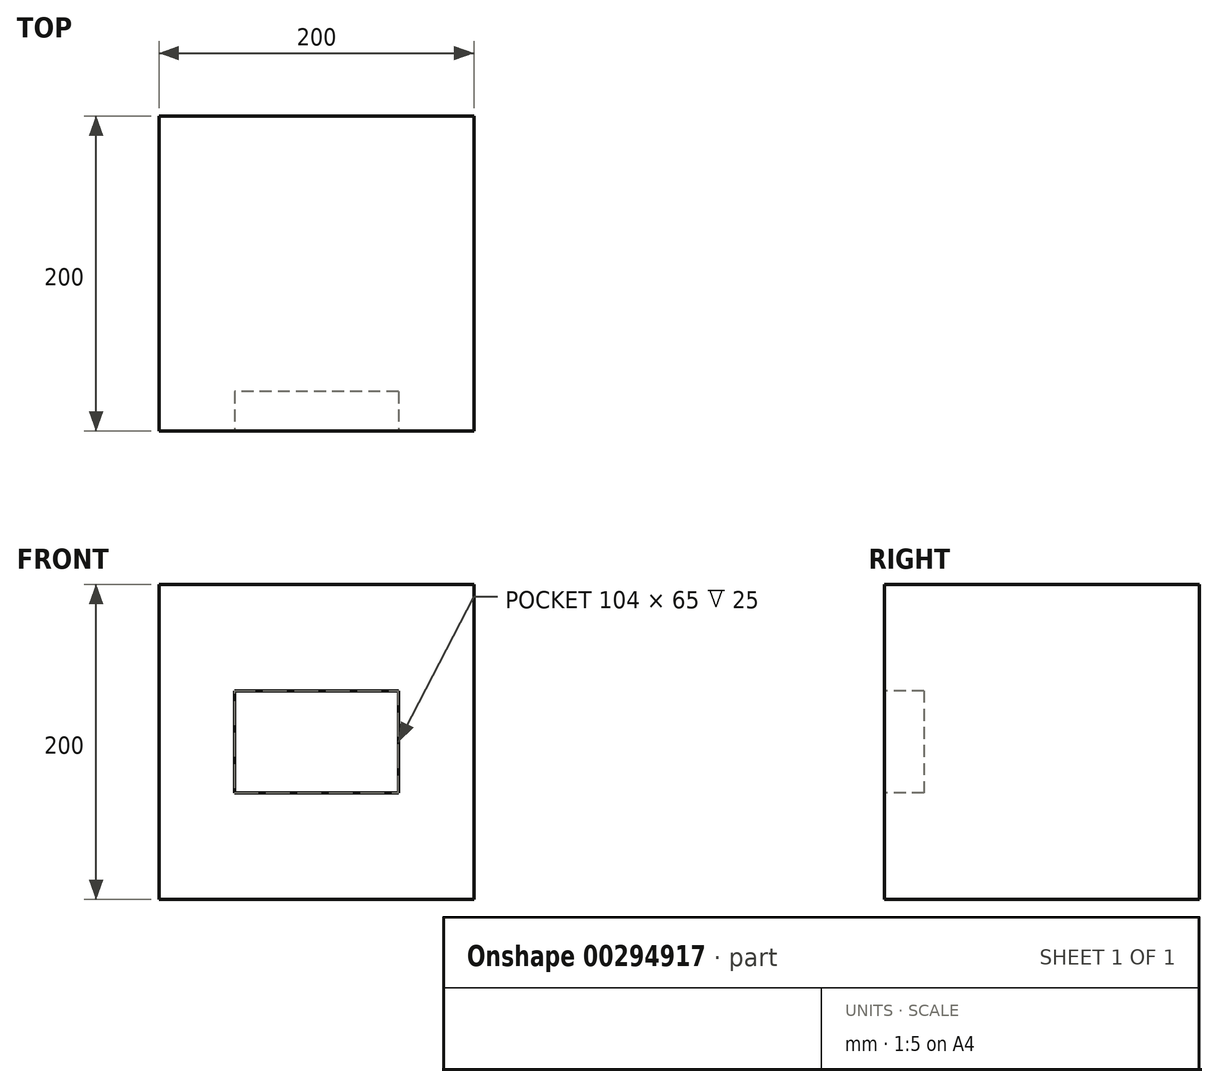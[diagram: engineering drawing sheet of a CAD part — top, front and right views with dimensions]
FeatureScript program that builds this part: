
annotation { "Feature Type Name" : "Feature", "Feature Type Description" : "" }
export const myFeature = defineFeature(function(context is Context, id is Id, definition is map)
    precondition{}
    {
        {
            var Q0;
            Q0=qCreatedBy(makeId("Front.planeOp"),FACE);
            var sketch = newSketch(context, id + "F0", { "sketchPlane" : qUnion([Q0])});
            skLineSegment(sketch, "E0.bottom", {"start": v(100, 100) * mm, "end": v(-100, 100) * mm});
            skLineSegment(sketch, "E0.top", {"start": v(100, -100) * mm, "end": v(-100, -100) * mm});
            skLineSegment(sketch, "E0.left", {"start": v(100, 100) * mm, "end": v(100, -100) * mm});
            skLineSegment(sketch, "E0.right", {"start": v(-100, 100) * mm, "end": v(-100, -100) * mm});
            skPoint(sketch, "E0.middle", {"position": v(0, 0) * mm});
            skSolve(sketch);
        }
        {
            var Q0;
            Q0=makeQuery(id+"F0.imprint","IMPRINT",FACE,{"disambiguationData":[TD([[makeQuery(id+"F0.imprint","IMPRINT",EDGE,{"derivedFrom":sQuery(id+"F0.wireOp",EDGE,"E0.bottom")}),1.0]])]});
            extrude(context, id + "F1", {"entities" : qUnion([Q0]), "depth" : 200 * mm, "offsetDistance" : 25 * mm});
        }
        {
            var Q0;
            Q0=makeQuery(id+"F1.opExtrude","CAP_FACE",FACE,{"disambiguationData":[OSD([sQuery(id+"F0.wireOp",EDGE,"E0.bottom"),sQuery(id+"F0.wireOp",EDGE,"E0.top"),sQuery(id+"F0.wireOp",EDGE,"E0.left"),sQuery(id+"F0.wireOp",EDGE,"E0.right")])],"isStart":false});
            var sketch = newSketch(context, id + "F2", { "sketchPlane" : qUnion([Q0])});
            skLineSegment(sketch, "E1.bottom", {"start": v(52, 32.5) * mm, "end": v(-52, 32.5) * mm});
            skLineSegment(sketch, "E1.top", {"start": v(52, -32.5) * mm, "end": v(-52, -32.5) * mm});
            skLineSegment(sketch, "E1.left", {"start": v(52, 32.5) * mm, "end": v(52, -32.5) * mm});
            skLineSegment(sketch, "E1.right", {"start": v(-52, 32.5) * mm, "end": v(-52, -32.5) * mm});
            skPoint(sketch, "E1.middle", {"position": v(0, 0) * mm});
            skSolve(sketch);
        }
        {
            var Q0;
            Q0=makeQuery(id+"F2.imprint","IMPRINT",FACE,{"disambiguationData":[TD([[makeQuery(id+"F2.imprint","IMPRINT",EDGE,{"derivedFrom":sQuery(id+"F2.wireOp",EDGE,"E1.bottom")}),1.0]])]});
            extrude(context, id + "F3", {"entities" : qUnion([Q0]), "operationType" : NewBodyOperationType.REMOVE, "oppositeDirection" : true, "depth" : 25 * mm, "offsetDistance" : 25 * mm});
        }
    });
